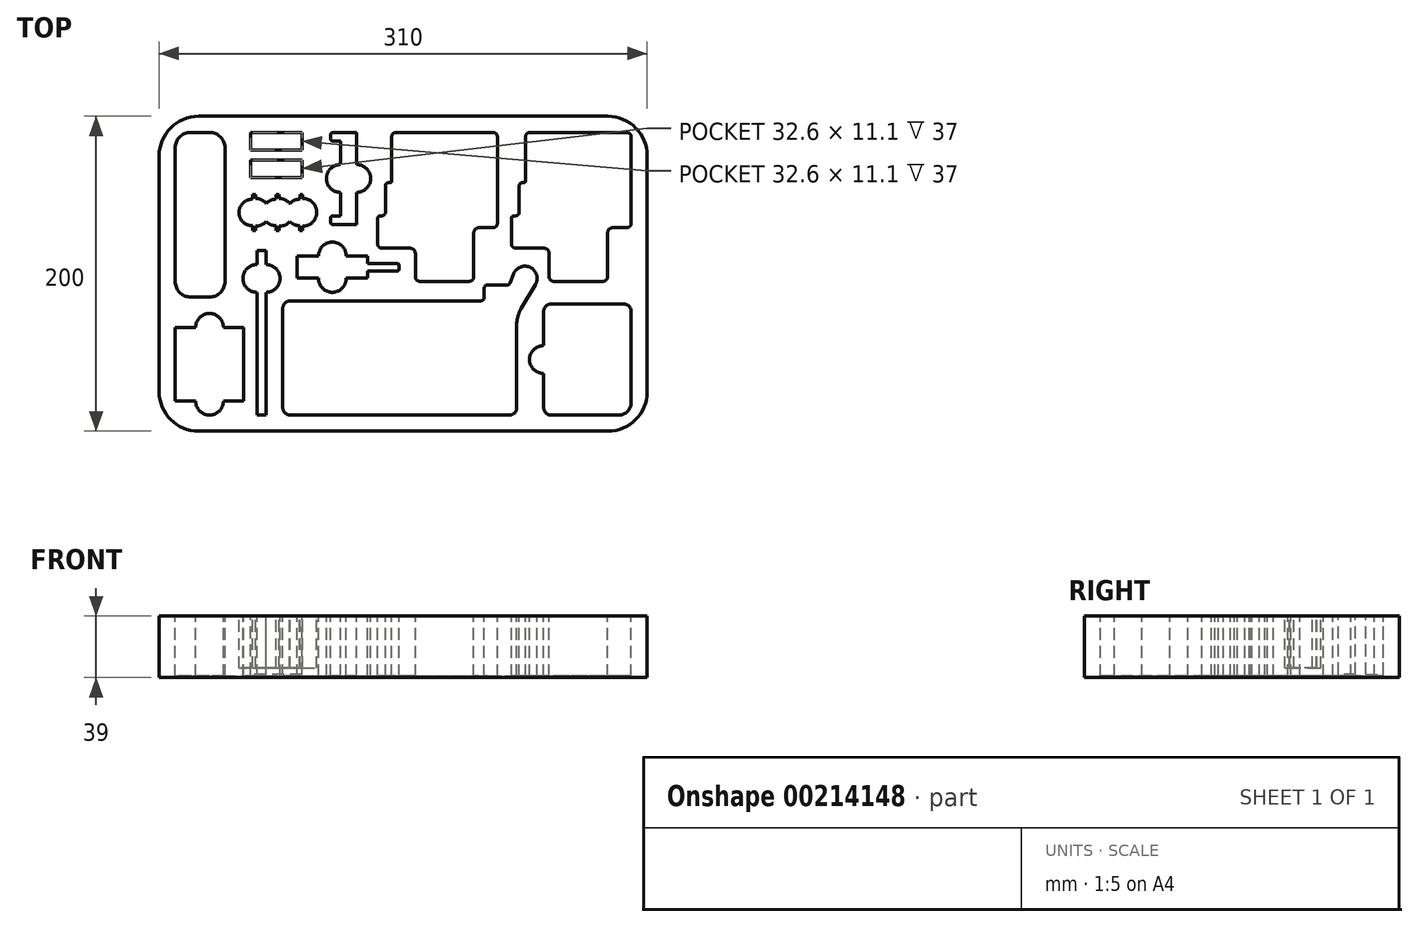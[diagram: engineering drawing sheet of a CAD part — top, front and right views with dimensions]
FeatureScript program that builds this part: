
annotation { "Feature Type Name" : "Feature", "Feature Type Description" : "" }
export const myFeature = defineFeature(function(context is Context, id is Id, definition is map)
    precondition{}
    {
        {
            var Q0;
            Q0=qCreatedBy(makeId("Top.planeOp"),FACE);
            var sketch = newSketch(context, id + "F0", { "sketchPlane" : qUnion([Q0])});
            skLineSegment(sketch, "E0.bottom", {"start": v(178, 118) * mm, "end": v(-82, 118) * mm});
            skLineSegment(sketch, "E0.top", {"start": v(178, -82) * mm, "end": v(-82, -82) * mm});
            skLineSegment(sketch, "E0.left", {"start": v(203, 93) * mm, "end": v(203, -57) * mm});
            skLineSegment(sketch, "E0.right", {"start": v(-107, 93) * mm, "end": v(-107, -57) * mm});
            skPoint(sketch, "E0.middle", {"position": v(0, 0) * mm});
            skPoint(sketch, "E1.visualSharp", {"position": v(-107, 118) * mm});
            skArc(sketch, "E1.filletArc", {"start": v(-82, 118) * mm, "mid": v(-99.68, 110.68) * mm, "end": v(-107, 93) * mm});
            skPoint(sketch, "E2.visualSharp", {"position": v(203, 118) * mm});
            skArc(sketch, "E2.filletArc", {"start": v(203, 93) * mm, "mid": v(195.68, 110.68) * mm, "end": v(178, 118) * mm});
            skPoint(sketch, "E3.visualSharp", {"position": v(-107, -82) * mm});
            skArc(sketch, "E3.filletArc", {"start": v(-107, -57) * mm, "mid": v(-99.68, -74.68) * mm, "end": v(-82, -82) * mm});
            skPoint(sketch, "E4.visualSharp", {"position": v(203, -82) * mm});
            skArc(sketch, "E4.filletArc", {"start": v(178, -82) * mm, "mid": v(195.68, -74.68) * mm, "end": v(203, -57) * mm});
            skSolve(sketch);
        }
        {
            var Q0;
            Q0=makeQuery(id+"F0.imprint","IMPRINT",FACE,{"disambiguationData":[TD([[makeQuery(id+"F0.imprint","IMPRINT",EDGE,{"derivedFrom":sQuery(id+"F0.wireOp",EDGE,"E0.bottom")}),1.0]])]});
            extrude(context, id + "F1", {"entities" : qUnion([Q0]), "oppositeDirection" : true, "depth" : 39 * mm});
        }
        {
            var Q0;
            Q0=makeQuery(id+"F1.opExtrude","CAP_FACE",FACE,{"disambiguationData":[OSD([sQuery(id+"F0.wireOp",EDGE,"E0.bottom"),sQuery(id+"F0.wireOp",EDGE,"E0.top"),sQuery(id+"F0.wireOp",EDGE,"E0.left"),sQuery(id+"F0.wireOp",EDGE,"E0.right"),sQuery(id+"F0.wireOp",EDGE,"E1.filletArc"),sQuery(id+"F0.wireOp",EDGE,"E2.filletArc"),sQuery(id+"F0.wireOp",EDGE,"E3.filletArc"),sQuery(id+"F0.wireOp",EDGE,"E4.filletArc")])],"isStart":true});
            var sketch = newSketch(context, id + "F2", { "sketchPlane" : qUnion([Q0])});
            skLineSegment(sketch, "E5.bottom", {"start": v(193, -64) * mm, "end": v(193, -6) * mm});
            skLineSegment(sketch, "E5.top", {"start": v(137, -67) * mm, "end": v(137, -45.5) * mm});
            skLineSegment(sketch, "E5.left", {"start": v(185, -72) * mm, "end": v(142, -72) * mm});
            skLineSegment(sketch, "E5.right", {"start": v(188, -1) * mm, "end": v(142, -1) * mm});
            skPoint(sketch, "E6.visualSharp", {"position": v(137, -72) * mm});
            skArc(sketch, "E6.filletArc", {"start": v(137, -67) * mm, "mid": v(138.46, -70.54) * mm, "end": v(142, -72) * mm});
            skPoint(sketch, "E7.visualSharp", {"position": v(193, -72) * mm});
            skArc(sketch, "E7.filletArc", {"start": v(185, -72) * mm, "mid": v(190.66, -69.66) * mm, "end": v(193, -64) * mm});
            skPoint(sketch, "E8.visualSharp", {"position": v(193, -1) * mm});
            skArc(sketch, "E8.filletArc", {"start": v(193, -6) * mm, "mid": v(191.54, -2.46) * mm, "end": v(188, -1) * mm});
            skPoint(sketch, "E9.visualSharp", {"position": v(137, -1) * mm});
            skArc(sketch, "E9.filletArc", {"start": v(142, -1) * mm, "mid": v(138.46, -2.46) * mm, "end": v(137, -6) * mm});
            skArc(sketch, "E10", {"start": v(137, -27.5) * mm, "mid": v(128, -36.5) * mm, "end": v(137, -45.5) * mm});
            skLineSegment(sketch, "E11.trimOffspring", {"start": v(137, -27.5) * mm, "end": v(137, -6) * mm});
            skArc(sketch, "E12.0", {"start": v(137.2, -27.7) * mm, "mid": v(128.2, -36.5) * mm, "end": v(137.2, -45.3) * mm});
            skLineSegment(sketch, "E12.1", {"start": v(137.2, -67) * mm, "end": v(137.2, -45.3) * mm});
            skLineSegment(sketch, "E12.2", {"start": v(137.2, -27.7) * mm, "end": v(137.2, -6) * mm});
            skArc(sketch, "E12.3", {"start": v(137.2, -67) * mm, "mid": v(138.6, -70.4) * mm, "end": v(142, -71.8) * mm});
            skLineSegment(sketch, "E12.4", {"start": v(185, -71.8) * mm, "end": v(142, -71.8) * mm});
            skArc(sketch, "E12.5", {"start": v(185, -71.8) * mm, "mid": v(190.52, -69.52) * mm, "end": v(192.8, -64) * mm});
            skArc(sketch, "E12.6", {"start": v(142, -1.2) * mm, "mid": v(138.6, -2.6) * mm, "end": v(137.2, -6) * mm});
            skLineSegment(sketch, "E12.7", {"start": v(188, -1.2) * mm, "end": v(142, -1.2) * mm});
            skArc(sketch, "E12.8", {"start": v(192.8, -6) * mm, "mid": v(191.4, -2.6) * mm, "end": v(188, -1.2) * mm});
            skLineSegment(sketch, "E12.9", {"start": v(192.8, -64) * mm, "end": v(192.8, -6) * mm});
            skSolve(sketch);
        }
        {
            var Q0;
            Q0=makeQuery(id+"F2.imprint","IMPRINT",FACE,{"disambiguationData":[TD([[makeQuery(id+"F2.imprint","IMPRINT",EDGE,{"derivedFrom":sQuery(id+"F2.wireOp",EDGE,"E12.0")}),1.0]])]});
            extrude(context, id + "F3", {"entities" : qUnion([Q0]), "operationType" : NewBodyOperationType.REMOVE, "oppositeDirection" : true, "depth" : 38 * mm});
        }
        {
            var Q0;
            Q0=makeQuery(id+"F1.opExtrude","CAP_FACE",FACE,{"disambiguationData":[OSD([sQuery(id+"F0.wireOp",EDGE,"E0.bottom"),sQuery(id+"F0.wireOp",EDGE,"E0.top"),sQuery(id+"F0.wireOp",EDGE,"E0.left"),sQuery(id+"F0.wireOp",EDGE,"E0.right"),sQuery(id+"F0.wireOp",EDGE,"E1.filletArc"),sQuery(id+"F0.wireOp",EDGE,"E2.filletArc"),sQuery(id+"F0.wireOp",EDGE,"E3.filletArc"),sQuery(id+"F0.wireOp",EDGE,"E4.filletArc")])],"isStart":true});
            var sketch = newSketch(context, id + "F4", { "sketchPlane" : qUnion([Q0])});
            skLineSegment(sketch, "E13.bottom", {"start": v(128.5, 108) * mm, "end": v(190, 108) * mm});
            skLineSegment(sketch, "E13.left", {"start": v(125.5, 105) * mm, "end": v(125.5, 77) * mm});
            skLineSegment(sketch, "E13.right", {"start": v(193, 105) * mm, "end": v(193, 50) * mm});
            skLineSegment(sketch, "E14.bottom", {"start": v(124.5, 76) * mm, "end": v(123.5, 76) * mm});
            skLineSegment(sketch, "E14.right", {"start": v(121.5, 74) * mm, "end": v(121.5, 57) * mm});
            skLineSegment(sketch, "E15.top", {"start": v(143.5, 13) * mm, "end": v(175, 13) * mm});
            skLineSegment(sketch, "E15.right", {"start": v(178, 44) * mm, "end": v(178, 16) * mm});
            skLineSegment(sketch, "E16.bottom", {"start": v(137.5, 34) * mm, "end": v(119.5, 34) * mm});
            skLineSegment(sketch, "E16.top", {"start": v(119.5, 55) * mm, "end": v(118.5, 55) * mm});
            skLineSegment(sketch, "E16.right", {"start": v(116.5, 37) * mm, "end": v(116.5, 53) * mm});
            skLineSegment(sketch, "E17.trimOffspring", {"start": v(140.5, 31) * mm, "end": v(140.5, 16) * mm});
            skLineSegment(sketch, "E18.trimOffspring", {"start": v(181, 47) * mm, "end": v(190, 47) * mm});
            skPoint(sketch, "E19.visualSharp", {"position": v(193, 108) * mm});
            skArc(sketch, "E19.filletArc", {"start": v(193, 105) * mm, "mid": v(192.12, 107.12) * mm, "end": v(190, 108) * mm});
            skPoint(sketch, "E20.visualSharp", {"position": v(193, 47) * mm});
            skArc(sketch, "E20.filletArc", {"start": v(190, 47) * mm, "mid": v(192.12, 47.88) * mm, "end": v(193, 50) * mm});
            skPoint(sketch, "E21.visualSharp", {"position": v(178, 47) * mm});
            skArc(sketch, "E21.filletArc", {"start": v(181, 47) * mm, "mid": v(178.88, 46.12) * mm, "end": v(178, 44) * mm});
            skPoint(sketch, "E22.visualSharp", {"position": v(178, 13) * mm});
            skArc(sketch, "E22.filletArc", {"start": v(175, 13) * mm, "mid": v(177.12, 13.88) * mm, "end": v(178, 16) * mm});
            skPoint(sketch, "E23.visualSharp", {"position": v(140.5, 13) * mm});
            skArc(sketch, "E23.filletArc", {"start": v(140.5, 16) * mm, "mid": v(141.38, 13.88) * mm, "end": v(143.5, 13) * mm});
            skPoint(sketch, "E24.visualSharp", {"position": v(140.5, 34) * mm});
            skArc(sketch, "E24.filletArc", {"start": v(140.5, 31) * mm, "mid": v(139.62, 33.12) * mm, "end": v(137.5, 34) * mm});
            skPoint(sketch, "E25.visualSharp", {"position": v(116.5, 34) * mm});
            skArc(sketch, "E25.filletArc", {"start": v(116.5, 37) * mm, "mid": v(117.38, 34.88) * mm, "end": v(119.5, 34) * mm});
            skPoint(sketch, "E26.visualSharp", {"position": v(116.5, 55) * mm});
            skArc(sketch, "E26.filletArc", {"start": v(118.5, 55) * mm, "mid": v(117.09, 54.41) * mm, "end": v(116.5, 53) * mm});
            skPoint(sketch, "E27.visualSharp", {"position": v(121.5, 76) * mm});
            skArc(sketch, "E27.filletArc", {"start": v(123.5, 76) * mm, "mid": v(122.09, 75.41) * mm, "end": v(121.5, 74) * mm});
            skPoint(sketch, "E28.visualSharp", {"position": v(125.5, 108) * mm});
            skArc(sketch, "E28.filletArc", {"start": v(128.5, 108) * mm, "mid": v(126.38, 107.12) * mm, "end": v(125.5, 105) * mm});
            skPoint(sketch, "E29.visualSharp", {"position": v(121.5, 55) * mm});
            skArc(sketch, "E29.filletArc", {"start": v(119.5, 55) * mm, "mid": v(120.91, 55.59) * mm, "end": v(121.5, 57) * mm});
            skPoint(sketch, "E30.visualSharp", {"position": v(125.5, 76) * mm});
            skArc(sketch, "E30.filletArc", {"start": v(124.5, 76) * mm, "mid": v(125.2, 76.3) * mm, "end": v(125.5, 77) * mm});
            skArc(sketch, "E31.0", {"start": v(128.5, 107.8) * mm, "mid": v(126.52, 106.98) * mm, "end": v(125.7, 105) * mm});
            skLineSegment(sketch, "E31.1", {"start": v(140.7, 31) * mm, "end": v(140.7, 16) * mm});
            skArc(sketch, "E31.2", {"start": v(140.7, 16) * mm, "mid": v(141.52, 14.02) * mm, "end": v(143.5, 13.2) * mm});
            skLineSegment(sketch, "E31.3", {"start": v(143.5, 13.2) * mm, "end": v(175, 13.2) * mm});
            skArc(sketch, "E31.4", {"start": v(175, 13.2) * mm, "mid": v(176.98, 14.02) * mm, "end": v(177.8, 16) * mm});
            skLineSegment(sketch, "E31.5", {"start": v(177.8, 44) * mm, "end": v(177.8, 16) * mm});
            skArc(sketch, "E31.6", {"start": v(181, 47.2) * mm, "mid": v(178.74, 46.26) * mm, "end": v(177.8, 44) * mm});
            skArc(sketch, "E31.7", {"start": v(192.8, 105) * mm, "mid": v(191.98, 106.98) * mm, "end": v(190, 107.8) * mm});
            skLineSegment(sketch, "E31.8", {"start": v(192.8, 105) * mm, "end": v(192.8, 50) * mm});
            skArc(sketch, "E31.9", {"start": v(190, 47.2) * mm, "mid": v(191.98, 48.02) * mm, "end": v(192.8, 50) * mm});
            skLineSegment(sketch, "E31.10", {"start": v(181, 47.2) * mm, "end": v(190, 47.2) * mm});
            skArc(sketch, "E31.11", {"start": v(140.7, 31) * mm, "mid": v(139.76, 33.26) * mm, "end": v(137.5, 34.2) * mm});
            skLineSegment(sketch, "E31.12", {"start": v(128.5, 107.8) * mm, "end": v(190, 107.8) * mm});
            skLineSegment(sketch, "E31.13", {"start": v(137.5, 34.2) * mm, "end": v(119.5, 34.2) * mm});
            skArc(sketch, "E31.14", {"start": v(116.7, 37) * mm, "mid": v(117.52, 35.02) * mm, "end": v(119.5, 34.2) * mm});
            skLineSegment(sketch, "E31.15", {"start": v(116.7, 37) * mm, "end": v(116.7, 53) * mm});
            skArc(sketch, "E31.16", {"start": v(118.5, 54.8) * mm, "mid": v(117.23, 54.27) * mm, "end": v(116.7, 53) * mm});
            skLineSegment(sketch, "E31.17", {"start": v(119.5, 54.8) * mm, "end": v(118.5, 54.8) * mm});
            skArc(sketch, "E31.18", {"start": v(119.5, 54.8) * mm, "mid": v(121.06, 55.44) * mm, "end": v(121.7, 57) * mm});
            skLineSegment(sketch, "E31.19", {"start": v(121.7, 74) * mm, "end": v(121.7, 57) * mm});
            skArc(sketch, "E31.20", {"start": v(123.5, 75.8) * mm, "mid": v(122.23, 75.27) * mm, "end": v(121.7, 74) * mm});
            skLineSegment(sketch, "E31.21", {"start": v(124.5, 75.8) * mm, "end": v(123.5, 75.8) * mm});
            skArc(sketch, "E31.22", {"start": v(124.5, 75.8) * mm, "mid": v(125.35, 76.15) * mm, "end": v(125.7, 77) * mm});
            skLineSegment(sketch, "E31.23", {"start": v(125.7, 105) * mm, "end": v(125.7, 77) * mm});
            skLineSegment(sketch, "E32.1.0.0", {"start": v(43.5, 107.8) * mm, "end": v(105, 107.8) * mm});
            skArc(sketch, "E32.1.0.1", {"start": v(43.5, 107.8) * mm, "mid": v(41.52, 106.98) * mm, "end": v(40.7, 105) * mm});
            skLineSegment(sketch, "E32.1.0.2", {"start": v(40.7, 105) * mm, "end": v(40.7, 77) * mm});
            skArc(sketch, "E32.1.0.3", {"start": v(39.5, 75.8) * mm, "mid": v(40.35, 76.15) * mm, "end": v(40.7, 77) * mm});
            skLineSegment(sketch, "E32.1.0.4", {"start": v(39.5, 75.8) * mm, "end": v(38.5, 75.8) * mm});
            skArc(sketch, "E32.1.0.5", {"start": v(38.5, 75.8) * mm, "mid": v(37.23, 75.27) * mm, "end": v(36.7, 74) * mm});
            skLineSegment(sketch, "E32.1.0.6", {"start": v(36.7, 74) * mm, "end": v(36.7, 57) * mm});
            skArc(sketch, "E32.1.0.7", {"start": v(34.5, 54.8) * mm, "mid": v(36.06, 55.44) * mm, "end": v(36.7, 57) * mm});
            skLineSegment(sketch, "E32.1.0.8", {"start": v(34.5, 54.8) * mm, "end": v(33.5, 54.8) * mm});
            skArc(sketch, "E32.1.0.9", {"start": v(33.5, 54.8) * mm, "mid": v(32.23, 54.27) * mm, "end": v(31.7, 53) * mm});
            skLineSegment(sketch, "E32.1.0.10", {"start": v(31.7, 37) * mm, "end": v(31.7, 53) * mm});
            skArc(sketch, "E32.1.0.11", {"start": v(31.7, 37) * mm, "mid": v(32.52, 35.02) * mm, "end": v(34.5, 34.2) * mm});
            skLineSegment(sketch, "E32.1.0.12", {"start": v(52.5, 34.2) * mm, "end": v(34.5, 34.2) * mm});
            skArc(sketch, "E32.1.0.13", {"start": v(55.7, 31) * mm, "mid": v(54.76, 33.26) * mm, "end": v(52.5, 34.2) * mm});
            skLineSegment(sketch, "E32.1.0.14", {"start": v(55.7, 31) * mm, "end": v(55.7, 16) * mm});
            skArc(sketch, "E32.1.0.15", {"start": v(55.7, 16) * mm, "mid": v(56.52, 14.02) * mm, "end": v(58.5, 13.2) * mm});
            skLineSegment(sketch, "E32.1.0.16", {"start": v(58.5, 13.2) * mm, "end": v(90, 13.2) * mm});
            skArc(sketch, "E32.1.0.17", {"start": v(90, 13.2) * mm, "mid": v(91.98, 14.02) * mm, "end": v(92.8, 16) * mm});
            skLineSegment(sketch, "E32.1.0.18", {"start": v(92.8, 44) * mm, "end": v(92.8, 16) * mm});
            skArc(sketch, "E32.1.0.19", {"start": v(96, 47.2) * mm, "mid": v(93.74, 46.26) * mm, "end": v(92.8, 44) * mm});
            skLineSegment(sketch, "E32.1.0.20", {"start": v(96, 47.2) * mm, "end": v(105, 47.2) * mm});
            skArc(sketch, "E32.1.0.21", {"start": v(105, 47.2) * mm, "mid": v(106.98, 48.02) * mm, "end": v(107.8, 50) * mm});
            skLineSegment(sketch, "E32.1.0.22", {"start": v(107.8, 105) * mm, "end": v(107.8, 50) * mm});
            skArc(sketch, "E32.1.0.23", {"start": v(107.8, 105) * mm, "mid": v(106.98, 106.98) * mm, "end": v(105, 107.8) * mm});
            skLineSegment(sketch, "E32.direction1", {"start": v(119.5, 34.2) * mm, "end": v(34.5, 34.2) * mm, "construction": true});
            skSolve(sketch);
        }
        {
            var Q0;
            Q0=makeQuery(id+"F4.imprint","IMPRINT",FACE,{"disambiguationData":[TD([[makeQuery(id+"F4.imprint","IMPRINT",EDGE,{"derivedFrom":sQuery(id+"F4.wireOp",EDGE,"E31.0")}),1.0]])]});
            var Q1;
            Q1=makeQuery(id+"F4.imprint","IMPRINT",FACE,{"disambiguationData":[TD([[makeQuery(id+"F4.imprint","IMPRINT",EDGE,{"derivedFrom":sQuery(id+"F4.wireOp",EDGE,"E32.1.0.0")}),-1.0]])]});
            extrude(context, id + "F5", {"entities" : qUnion([Q0, Q1]), "operationType" : NewBodyOperationType.REMOVE, "oppositeDirection" : true, "depth" : 38 * mm});
        }
        {
            var Q0;
            Q0=makeQuery(id+"F1.opExtrude","CAP_FACE",FACE,{"disambiguationData":[OSD([sQuery(id+"F0.wireOp",EDGE,"E0.bottom"),sQuery(id+"F0.wireOp",EDGE,"E0.top"),sQuery(id+"F0.wireOp",EDGE,"E0.left"),sQuery(id+"F0.wireOp",EDGE,"E0.right"),sQuery(id+"F0.wireOp",EDGE,"E1.filletArc"),sQuery(id+"F0.wireOp",EDGE,"E2.filletArc"),sQuery(id+"F0.wireOp",EDGE,"E3.filletArc"),sQuery(id+"F0.wireOp",EDGE,"E4.filletArc")])],"isStart":true});
            var sketch = newSketch(context, id + "F6", { "sketchPlane" : qUnion([Q0])});
            skLineSegment(sketch, "E33.bottom", {"start": v(-19.5, 15) * mm, "end": v(-6, 15) * mm});
            skLineSegment(sketch, "E33.top", {"start": v(-19.5, 29.3) * mm, "end": v(-6, 29.3) * mm});
            skLineSegment(sketch, "E33.left", {"start": v(-19.5, 15) * mm, "end": v(-19.5, 29.3) * mm});
            skLineSegment(sketch, "E33.right", {"start": v(25.5, 15) * mm, "end": v(25.5, 19.65) * mm});
            skLineSegment(sketch, "E34.bottom", {"start": v(25.5, 19.65) * mm, "end": v(44.5, 19.65) * mm});
            skLineSegment(sketch, "E34.top", {"start": v(25.5, 24.65) * mm, "end": v(44.5, 24.65) * mm});
            skLineSegment(sketch, "E34.right", {"start": v(45.5, 20.65) * mm, "end": v(45.5, 23.65) * mm});
            skLineSegment(sketch, "E35.trimOffspring", {"start": v(25.5, 24.65) * mm, "end": v(25.5, 29.3) * mm});
            skArc(sketch, "E36", {"start": v(12, 29.3) * mm, "mid": v(3, 38.3) * mm, "end": v(-6, 29.3) * mm});
            skArc(sketch, "E37", {"start": v(-6, 15) * mm, "mid": v(3, 6) * mm, "end": v(12, 15) * mm});
            skPoint(sketch, "E38.visualSharp", {"position": v(45.5, 24.65) * mm});
            skArc(sketch, "E38.filletArc", {"start": v(45.5, 23.65) * mm, "mid": v(45.2, 24.36) * mm, "end": v(44.5, 24.65) * mm});
            skPoint(sketch, "E39.visualSharp", {"position": v(45.5, 19.65) * mm});
            skArc(sketch, "E39.filletArc", {"start": v(44.5, 19.65) * mm, "mid": v(45.2, 19.94) * mm, "end": v(45.5, 20.65) * mm});
            skLineSegment(sketch, "E40.trimOffspring", {"start": v(12, 29.3) * mm, "end": v(25.5, 29.3) * mm});
            skLineSegment(sketch, "E41.trimOffspring", {"start": v(12, 15) * mm, "end": v(25.5, 15) * mm});
            skLineSegment(sketch, "E42.0", {"start": v(11.8, 29.1) * mm, "end": v(25.3, 29.1) * mm});
            skLineSegment(sketch, "E42.1", {"start": v(25.3, 24.45) * mm, "end": v(25.3, 29.1) * mm});
            skLineSegment(sketch, "E42.2", {"start": v(25.3, 24.45) * mm, "end": v(44.5, 24.45) * mm});
            skArc(sketch, "E42.3", {"start": v(-5.8, 15.2) * mm, "mid": v(3, 6.2) * mm, "end": v(11.8, 15.2) * mm});
            skLineSegment(sketch, "E42.4", {"start": v(-19.3, 15.2) * mm, "end": v(-5.8, 15.2) * mm});
            skLineSegment(sketch, "E42.5", {"start": v(-19.3, 15.2) * mm, "end": v(-19.3, 29.1) * mm});
            skLineSegment(sketch, "E42.6", {"start": v(-19.3, 29.1) * mm, "end": v(-5.8, 29.1) * mm});
            skLineSegment(sketch, "E42.7", {"start": v(11.8, 15.2) * mm, "end": v(25.3, 15.2) * mm});
            skLineSegment(sketch, "E42.8", {"start": v(25.3, 15.2) * mm, "end": v(25.3, 19.85) * mm});
            skLineSegment(sketch, "E42.9", {"start": v(25.3, 19.85) * mm, "end": v(44.5, 19.85) * mm});
            skArc(sketch, "E42.10", {"start": v(11.8, 29.1) * mm, "mid": v(3, 38.1) * mm, "end": v(-5.8, 29.1) * mm});
            skArc(sketch, "E42.11", {"start": v(44.5, 19.85) * mm, "mid": v(45.07, 20.08) * mm, "end": v(45.3, 20.65) * mm});
            skLineSegment(sketch, "E42.12", {"start": v(45.3, 20.65) * mm, "end": v(45.3, 23.65) * mm});
            skArc(sketch, "E42.13", {"start": v(45.3, 23.65) * mm, "mid": v(45.07, 24.22) * mm, "end": v(44.5, 24.45) * mm});
            skSolve(sketch);
        }
        {
            var Q0;
            Q0=makeQuery(id+"F6.imprint","IMPRINT",FACE,{"disambiguationData":[TD([[makeQuery(id+"F6.imprint","IMPRINT",EDGE,{"derivedFrom":sQuery(id+"F6.wireOp",EDGE,"E42.0")}),-1.0]])]});
            extrude(context, id + "F7", {"entities" : qUnion([Q0]), "operationType" : NewBodyOperationType.REMOVE, "oppositeDirection" : true, "depth" : 38 * mm});
        }
        {
            var Q0;
            Q0=makeQuery(id+"F1.opExtrude","CAP_FACE",FACE,{"disambiguationData":[OSD([sQuery(id+"F0.wireOp",EDGE,"E0.bottom"),sQuery(id+"F0.wireOp",EDGE,"E0.top"),sQuery(id+"F0.wireOp",EDGE,"E0.left"),sQuery(id+"F0.wireOp",EDGE,"E0.right"),sQuery(id+"F0.wireOp",EDGE,"E1.filletArc"),sQuery(id+"F0.wireOp",EDGE,"E2.filletArc"),sQuery(id+"F0.wireOp",EDGE,"E3.filletArc"),sQuery(id+"F0.wireOp",EDGE,"E4.filletArc")])],"isStart":true});
            var sketch = newSketch(context, id + "F8", { "sketchPlane" : qUnion([Q0])});
            skLineSegment(sketch, "E43.bottom", {"start": v(-45, 33) * mm, "end": v(-45, 24) * mm});
            skLineSegment(sketch, "E43.top", {"start": v(-39, 33) * mm, "end": v(-39, 24) * mm});
            skLineSegment(sketch, "E43.left", {"start": v(-45, 33) * mm, "end": v(-39, 33) * mm});
            skLineSegment(sketch, "E43.right", {"start": v(-45, -72) * mm, "end": v(-39, -72) * mm});
            skArc(sketch, "E44", {"start": v(-39, 6) * mm, "mid": v(-30, 15) * mm, "end": v(-39, 24) * mm});
            skArc(sketch, "E45", {"start": v(-45, 24) * mm, "mid": v(-54, 15) * mm, "end": v(-45, 6) * mm});
            skLineSegment(sketch, "E46.trimOffspring", {"start": v(-45, 6) * mm, "end": v(-45, -72) * mm});
            skLineSegment(sketch, "E47.trimOffspring", {"start": v(-39, 6) * mm, "end": v(-39, -72) * mm});
            skLineSegment(sketch, "E48.0", {"start": v(-44.8, 32.8) * mm, "end": v(-44.8, 23.8) * mm});
            skArc(sketch, "E48.1", {"start": v(-44.8, 23.8) * mm, "mid": v(-53.8, 15) * mm, "end": v(-44.8, 6.2) * mm});
            skLineSegment(sketch, "E48.2", {"start": v(-44.8, 32.8) * mm, "end": v(-39.2, 32.8) * mm});
            skLineSegment(sketch, "E48.3", {"start": v(-44.8, 6.2) * mm, "end": v(-44.8, -71.8) * mm});
            skLineSegment(sketch, "E48.4", {"start": v(-39.2, 32.8) * mm, "end": v(-39.2, 23.8) * mm});
            skArc(sketch, "E48.5", {"start": v(-39.2, 6.2) * mm, "mid": v(-30.2, 15) * mm, "end": v(-39.2, 23.8) * mm});
            skLineSegment(sketch, "E48.6", {"start": v(-39.2, 6.2) * mm, "end": v(-39.2, -71.8) * mm});
            skLineSegment(sketch, "E48.7", {"start": v(-44.8, -71.8) * mm, "end": v(-39.2, -71.8) * mm});
            skSolve(sketch);
        }
        {
            var Q0;
            Q0=makeQuery(id+"F8.imprint","IMPRINT",FACE,{"disambiguationData":[TD([[makeQuery(id+"F8.imprint","IMPRINT",EDGE,{"derivedFrom":sQuery(id+"F8.wireOp",EDGE,"E48.0")}),1.0]])]});
            extrude(context, id + "F9", {"entities" : qUnion([Q0]), "operationType" : NewBodyOperationType.REMOVE, "oppositeDirection" : true, "depth" : 38 * mm});
        }
        {
            var Q0;
            Q0=makeQuery(id+"F1.opExtrude","CAP_FACE",FACE,{"disambiguationData":[OSD([sQuery(id+"F0.wireOp",EDGE,"E0.bottom"),sQuery(id+"F0.wireOp",EDGE,"E0.top"),sQuery(id+"F0.wireOp",EDGE,"E0.left"),sQuery(id+"F0.wireOp",EDGE,"E0.right"),sQuery(id+"F0.wireOp",EDGE,"E1.filletArc"),sQuery(id+"F0.wireOp",EDGE,"E2.filletArc"),sQuery(id+"F0.wireOp",EDGE,"E3.filletArc"),sQuery(id+"F0.wireOp",EDGE,"E4.filletArc")])],"isStart":true});
            var sketch = newSketch(context, id + "F10", { "sketchPlane" : qUnion([Q0])});
            skLineSegment(sketch, "E49.bottom", {"start": v(-65, 13) * mm, "end": v(-65, 98) * mm});
            skLineSegment(sketch, "E49.top", {"start": v(-97, 13) * mm, "end": v(-97, 98) * mm});
            skLineSegment(sketch, "E49.left", {"start": v(-75, 3) * mm, "end": v(-87, 3) * mm});
            skLineSegment(sketch, "E49.right", {"start": v(-75, 108) * mm, "end": v(-87, 108) * mm});
            skPoint(sketch, "E50.visualSharp", {"position": v(-97, 108) * mm});
            skArc(sketch, "E50.filletArc", {"start": v(-87, 108) * mm, "mid": v(-94.07, 105.07) * mm, "end": v(-97, 98) * mm});
            skPoint(sketch, "E51.visualSharp", {"position": v(-65, 108) * mm});
            skArc(sketch, "E51.filletArc", {"start": v(-65, 98) * mm, "mid": v(-67.93, 105.07) * mm, "end": v(-75, 108) * mm});
            skPoint(sketch, "E52.visualSharp", {"position": v(-65, 3) * mm});
            skArc(sketch, "E52.filletArc", {"start": v(-75, 3) * mm, "mid": v(-67.93, 5.93) * mm, "end": v(-65, 13) * mm});
            skPoint(sketch, "E53.visualSharp", {"position": v(-97, 3) * mm});
            skArc(sketch, "E53.filletArc", {"start": v(-97, 13) * mm, "mid": v(-94.07, 5.93) * mm, "end": v(-87, 3) * mm});
            skArc(sketch, "E54.0", {"start": v(-65.2, 98) * mm, "mid": v(-68.07, 104.93) * mm, "end": v(-75, 107.8) * mm});
            skLineSegment(sketch, "E54.1", {"start": v(-65.2, 13) * mm, "end": v(-65.2, 98) * mm});
            skLineSegment(sketch, "E54.2", {"start": v(-75, 107.8) * mm, "end": v(-87, 107.8) * mm});
            skArc(sketch, "E54.3", {"start": v(-75, 3.2) * mm, "mid": v(-68.07, 6.07) * mm, "end": v(-65.2, 13) * mm});
            skArc(sketch, "E54.4", {"start": v(-87, 107.8) * mm, "mid": v(-93.93, 104.93) * mm, "end": v(-96.8, 98) * mm});
            skLineSegment(sketch, "E54.5", {"start": v(-96.8, 13) * mm, "end": v(-96.8, 98) * mm});
            skArc(sketch, "E54.6", {"start": v(-96.8, 13) * mm, "mid": v(-93.93, 6.07) * mm, "end": v(-87, 3.2) * mm});
            skLineSegment(sketch, "E54.7", {"start": v(-75, 3.2) * mm, "end": v(-87, 3.2) * mm});
            skSolve(sketch);
        }
        {
            var Q0;
            Q0=makeQuery(id+"F10.imprint","IMPRINT",FACE,{"disambiguationData":[TD([[makeQuery(id+"F10.imprint","IMPRINT",EDGE,{"derivedFrom":sQuery(id+"F10.wireOp",EDGE,"E54.0")}),1.0]])]});
            extrude(context, id + "F11", {"entities" : qUnion([Q0]), "operationType" : NewBodyOperationType.REMOVE, "oppositeDirection" : true, "depth" : 38 * mm});
        }
        {
            var Q0;
            Q0=makeQuery(id+"F1.opExtrude","CAP_FACE",FACE,{"disambiguationData":[OSD([sQuery(id+"F0.wireOp",EDGE,"E0.bottom"),sQuery(id+"F0.wireOp",EDGE,"E0.top"),sQuery(id+"F0.wireOp",EDGE,"E0.left"),sQuery(id+"F0.wireOp",EDGE,"E0.right"),sQuery(id+"F0.wireOp",EDGE,"E1.filletArc"),sQuery(id+"F0.wireOp",EDGE,"E2.filletArc"),sQuery(id+"F0.wireOp",EDGE,"E3.filletArc"),sQuery(id+"F0.wireOp",EDGE,"E4.filletArc")])],"isStart":true});
            var sketch = newSketch(context, id + "F12", { "sketchPlane" : qUnion([Q0])});
            skArc(sketch, "E55.MirrorCS", {"start": v(-45.7, 66) * mm, "mid": v(-42.02, 65.21) * mm, "end": v(-38.98, 62.99) * mm});
            skLineSegment(sketch, "E56.MirrorCS", {"start": v(-45.7, 45) * mm, "end": v(-45.7, 48) * mm});
            skLineSegment(sketch, "E57.MirrorCS", {"start": v(-47.95, 45) * mm, "end": v(-47.93, 48.33) * mm});
            skLineSegment(sketch, "E58.MirrorCS", {"start": v(-48.2, 68.53) * mm, "end": v(-45.9, 68.53) * mm});
            skLineSegment(sketch, "E59.MirrorCS", {"start": v(-48.35, 45.33) * mm, "end": v(-46.05, 45.33) * mm});
            skArc(sketch, "E60.MirrorCS", {"start": v(-47.93, 48.33) * mm, "mid": v(-56.47, 56.99) * mm, "end": v(-47.82, 65.53) * mm});
            skLineSegment(sketch, "E61.1.0.0", {"start": v(-30.7, 45) * mm, "end": v(-30.7, 48) * mm});
            skLineSegment(sketch, "E61.1.0.1", {"start": v(-32.95, 45) * mm, "end": v(-32.93, 48.33) * mm});
            skArc(sketch, "E61.1.0.2", {"start": v(-32.93, 48.33) * mm, "mid": v(-36.25, 49.02) * mm, "end": v(-39.04, 50.94) * mm});
            skArc(sketch, "E61.1.0.3", {"start": v(-30.7, 66) * mm, "mid": v(-27.02, 65.21) * mm, "end": v(-23.98, 62.99) * mm});
            skLineSegment(sketch, "E61.1.0.4", {"start": v(-33.2, 68.53) * mm, "end": v(-30.9, 68.53) * mm});
            skLineSegment(sketch, "E61.1.0.5", {"start": v(-33.35, 45.33) * mm, "end": v(-31.05, 45.33) * mm});
            skLineSegment(sketch, "E61.2.0.0", {"start": v(-15.7, 45) * mm, "end": v(-15.7, 48) * mm});
            skLineSegment(sketch, "E61.2.0.1", {"start": v(-17.95, 45) * mm, "end": v(-17.93, 48.33) * mm});
            skArc(sketch, "E61.2.0.2", {"start": v(-17.93, 48.33) * mm, "mid": v(-21.25, 49.02) * mm, "end": v(-24.04, 50.94) * mm});
            skArc(sketch, "E61.2.0.3", {"start": v(-15.7, 66) * mm, "mid": v(-6.7, 57) * mm, "end": v(-15.7, 48) * mm});
            skLineSegment(sketch, "E61.2.0.4", {"start": v(-18.2, 68.53) * mm, "end": v(-15.9, 68.53) * mm});
            skLineSegment(sketch, "E61.2.0.5", {"start": v(-18.35, 45.33) * mm, "end": v(-16.05, 45.33) * mm});
            skLineSegment(sketch, "E61.direction1", {"start": v(-47.95, 45) * mm, "end": v(-32.95, 45) * mm, "construction": true});
            skLineSegment(sketch, "E62.trimOffspring", {"start": v(-47.82, 65.53) * mm, "end": v(-47.8, 68.93) * mm});
            skLineSegment(sketch, "E63.trimOffspring", {"start": v(-45.7, 66) * mm, "end": v(-45.7, 69) * mm});
            skArc(sketch, "E64.trimOffspring", {"start": v(-38.98, 62.99) * mm, "mid": v(-36.16, 64.88) * mm, "end": v(-32.82, 65.53) * mm});
            skArc(sketch, "E65.trimOffspring", {"start": v(-39.04, 50.94) * mm, "mid": v(-42.06, 48.77) * mm, "end": v(-45.7, 48) * mm});
            skLineSegment(sketch, "E66.trimOffspring", {"start": v(-32.82, 65.53) * mm, "end": v(-32.8, 68.93) * mm});
            skLineSegment(sketch, "E67.trimOffspring", {"start": v(-30.7, 66) * mm, "end": v(-30.7, 69) * mm});
            skArc(sketch, "E68.trimOffspring", {"start": v(-23.98, 62.99) * mm, "mid": v(-21.16, 64.88) * mm, "end": v(-17.82, 65.53) * mm});
            skArc(sketch, "E69.trimOffspring", {"start": v(-24.04, 50.94) * mm, "mid": v(-27.06, 48.77) * mm, "end": v(-30.7, 48) * mm});
            skLineSegment(sketch, "E70.trimOffspring", {"start": v(-17.82, 65.53) * mm, "end": v(-17.8, 68.93) * mm});
            skLineSegment(sketch, "E71.trimOffspring", {"start": v(-15.7, 66) * mm, "end": v(-15.7, 69) * mm});
            skArc(sketch, "E72.0", {"start": v(-17.73, 48.54) * mm, "mid": v(-21.18, 49.21) * mm, "end": v(-24.05, 51.24) * mm});
            skLineSegment(sketch, "E72.1", {"start": v(-17.75, 45.53) * mm, "end": v(-17.73, 48.54) * mm});
            skLineSegment(sketch, "E72.2", {"start": v(-17.75, 45.53) * mm, "end": v(-15.9, 45.53) * mm});
            skLineSegment(sketch, "E72.3", {"start": v(-15.9, 45.53) * mm, "end": v(-15.9, 48.2) * mm});
            skArc(sketch, "E72.4", {"start": v(-15.9, 65.8) * mm, "mid": v(-6.9, 57) * mm, "end": v(-15.9, 48.2) * mm});
            skLineSegment(sketch, "E72.5", {"start": v(-47.62, 65.33) * mm, "end": v(-47.6, 68.33) * mm});
            skArc(sketch, "E72.6", {"start": v(-47.73, 48.54) * mm, "mid": v(-56.27, 56.99) * mm, "end": v(-47.62, 65.33) * mm});
            skLineSegment(sketch, "E72.7", {"start": v(-47.75, 45.53) * mm, "end": v(-47.73, 48.54) * mm});
            skLineSegment(sketch, "E72.8", {"start": v(-47.75, 45.53) * mm, "end": v(-45.9, 45.53) * mm});
            skLineSegment(sketch, "E72.9", {"start": v(-45.9, 45.53) * mm, "end": v(-45.9, 48.2) * mm});
            skArc(sketch, "E72.10", {"start": v(-39.05, 51.24) * mm, "mid": v(-42.13, 48.95) * mm, "end": v(-45.9, 48.2) * mm});
            skLineSegment(sketch, "E72.11", {"start": v(-30.9, 45.53) * mm, "end": v(-30.9, 48.2) * mm});
            skLineSegment(sketch, "E72.12", {"start": v(-32.75, 45.53) * mm, "end": v(-30.9, 45.53) * mm});
            skLineSegment(sketch, "E72.13", {"start": v(-32.75, 45.53) * mm, "end": v(-32.73, 48.54) * mm});
            skArc(sketch, "E72.14", {"start": v(-32.73, 48.54) * mm, "mid": v(-36.18, 49.21) * mm, "end": v(-39.05, 51.24) * mm});
            skLineSegment(sketch, "E72.15", {"start": v(-47.6, 68.33) * mm, "end": v(-45.9, 68.33) * mm});
            skLineSegment(sketch, "E72.16", {"start": v(-45.9, 65.8) * mm, "end": v(-45.9, 68.33) * mm});
            skArc(sketch, "E72.17", {"start": v(-45.9, 65.8) * mm, "mid": v(-42.1, 65.03) * mm, "end": v(-38.99, 62.7) * mm});
            skArc(sketch, "E72.18", {"start": v(-38.99, 62.7) * mm, "mid": v(-36.09, 64.7) * mm, "end": v(-32.62, 65.33) * mm});
            skLineSegment(sketch, "E72.19", {"start": v(-32.62, 65.33) * mm, "end": v(-32.6, 68.33) * mm});
            skArc(sketch, "E72.20", {"start": v(-24.05, 51.24) * mm, "mid": v(-27.13, 48.95) * mm, "end": v(-30.9, 48.2) * mm});
            skLineSegment(sketch, "E72.21", {"start": v(-32.6, 68.33) * mm, "end": v(-30.9, 68.33) * mm});
            skLineSegment(sketch, "E72.22", {"start": v(-30.9, 65.8) * mm, "end": v(-30.9, 68.33) * mm});
            skArc(sketch, "E72.23", {"start": v(-30.9, 65.8) * mm, "mid": v(-27.1, 65.03) * mm, "end": v(-23.99, 62.7) * mm});
            skArc(sketch, "E72.24", {"start": v(-23.99, 62.7) * mm, "mid": v(-21.09, 64.7) * mm, "end": v(-17.62, 65.33) * mm});
            skLineSegment(sketch, "E72.25", {"start": v(-17.62, 65.33) * mm, "end": v(-17.6, 68.33) * mm});
            skLineSegment(sketch, "E72.26", {"start": v(-17.6, 68.33) * mm, "end": v(-15.9, 68.33) * mm});
            skLineSegment(sketch, "E72.27", {"start": v(-15.9, 65.8) * mm, "end": v(-15.9, 68.33) * mm});
            skSolve(sketch);
        }
        {
            var Q0;
            Q0 = qSketchRegion(id + "F12", true);
            extrude(context, id + "F13", {"entities" : qUnion([Q0]), "operationType" : NewBodyOperationType.REMOVE, "oppositeDirection" : true, "depth" : 33 * mm});
        }
        {
            var Q0;
            Q0=makeQuery(id+"F1.opExtrude","CAP_FACE",FACE,{"disambiguationData":[OSD([sQuery(id+"F0.wireOp",EDGE,"E0.bottom"),sQuery(id+"F0.wireOp",EDGE,"E0.top"),sQuery(id+"F0.wireOp",EDGE,"E0.left"),sQuery(id+"F0.wireOp",EDGE,"E0.right"),sQuery(id+"F0.wireOp",EDGE,"E1.filletArc"),sQuery(id+"F0.wireOp",EDGE,"E2.filletArc"),sQuery(id+"F0.wireOp",EDGE,"E3.filletArc"),sQuery(id+"F0.wireOp",EDGE,"E4.filletArc")])],"isStart":true});
            var sketch = newSketch(context, id + "F14", { "sketchPlane" : qUnion([Q0])});
            skLineSegment(sketch, "E73.bottom", {"start": v(-16, 90.5) * mm, "end": v(-49, 90.5) * mm});
            skLineSegment(sketch, "E73.top", {"start": v(-16, 79) * mm, "end": v(-49, 79) * mm});
            skLineSegment(sketch, "E73.left", {"start": v(-16, 90.5) * mm, "end": v(-16, 79) * mm});
            skLineSegment(sketch, "E73.right", {"start": v(-49, 90.5) * mm, "end": v(-49, 79) * mm});
            skLineSegment(sketch, "E74", {"start": v(-16, 90.5) * mm, "end": v(-16, 93.5) * mm, "construction": true});
            skLineSegment(sketch, "E75", {"start": v(-16, 93.5) * mm, "end": v(-49, 93.5) * mm, "construction": true});
            skLineSegment(sketch, "E76", {"start": v(-49, 93.5) * mm, "end": v(-49, 90.5) * mm, "construction": true});
            skLineSegment(sketch, "E77.MirrorCS", {"start": v(-16, 96.5) * mm, "end": v(-49, 96.5) * mm});
            skLineSegment(sketch, "E78.MirrorCS", {"start": v(-16, 108) * mm, "end": v(-49, 108) * mm});
            skLineSegment(sketch, "E79.MirrorCS", {"start": v(-16, 96.5) * mm, "end": v(-16, 108) * mm});
            skLineSegment(sketch, "E80.MirrorCS", {"start": v(-49, 96.5) * mm, "end": v(-49, 108) * mm});
            skLineSegment(sketch, "E81.0", {"start": v(-16.2, 107.8) * mm, "end": v(-48.8, 107.8) * mm});
            skLineSegment(sketch, "E81.1", {"start": v(-16.2, 96.7) * mm, "end": v(-16.2, 107.8) * mm});
            skLineSegment(sketch, "E81.2", {"start": v(-16.2, 96.7) * mm, "end": v(-48.8, 96.7) * mm});
            skLineSegment(sketch, "E81.3", {"start": v(-48.8, 96.7) * mm, "end": v(-48.8, 107.8) * mm});
            skLineSegment(sketch, "E82.0", {"start": v(-16.2, 90.3) * mm, "end": v(-48.8, 90.3) * mm});
            skLineSegment(sketch, "E82.1", {"start": v(-16.2, 90.3) * mm, "end": v(-16.2, 79.2) * mm});
            skLineSegment(sketch, "E82.2", {"start": v(-16.2, 79.2) * mm, "end": v(-48.8, 79.2) * mm});
            skLineSegment(sketch, "E82.3", {"start": v(-48.8, 90.3) * mm, "end": v(-48.8, 79.2) * mm});
            skSolve(sketch);
        }
        {
            var Q0;
            Q0=makeQuery(id+"F14.imprint","IMPRINT",FACE,{"disambiguationData":[TD([[makeQuery(id+"F14.imprint","IMPRINT",EDGE,{"derivedFrom":sQuery(id+"F14.wireOp",EDGE,"E81.0")}),1.0]])]});
            var Q1;
            Q1=makeQuery(id+"F14.imprint","IMPRINT",FACE,{"disambiguationData":[TD([[makeQuery(id+"F14.imprint","IMPRINT",EDGE,{"derivedFrom":sQuery(id+"F14.wireOp",EDGE,"E82.0")}),1.0]])]});
            extrude(context, id + "F15", {"entities" : qUnion([Q0, Q1]), "operationType" : NewBodyOperationType.REMOVE, "oppositeDirection" : true, "depth" : 37 * mm});
        }
        {
            var Q0;
            Q0=makeQuery(id+"F1.opExtrude","CAP_FACE",FACE,{"disambiguationData":[OSD([sQuery(id+"F0.wireOp",EDGE,"E0.bottom"),sQuery(id+"F0.wireOp",EDGE,"E0.top"),sQuery(id+"F0.wireOp",EDGE,"E0.left"),sQuery(id+"F0.wireOp",EDGE,"E0.right"),sQuery(id+"F0.wireOp",EDGE,"E1.filletArc"),sQuery(id+"F0.wireOp",EDGE,"E2.filletArc"),sQuery(id+"F0.wireOp",EDGE,"E3.filletArc"),sQuery(id+"F0.wireOp",EDGE,"E4.filletArc")])],"isStart":true});
            var sketch = newSketch(context, id + "F16", { "sketchPlane" : qUnion([Q0])});
            skLineSegment(sketch, "E83.bottom", {"start": v(18.53, 87.5) * mm, "end": v(18.53, 108) * mm});
            skLineSegment(sketch, "E83.top", {"start": v(8.03, 87.5) * mm, "end": v(8.03, 102) * mm});
            skLineSegment(sketch, "E83.right", {"start": v(18.53, 108) * mm, "end": v(3.53, 108) * mm});
            skLineSegment(sketch, "E84.top", {"start": v(1.53, 106) * mm, "end": v(1.53, 104) * mm});
            skLineSegment(sketch, "E84.right", {"start": v(8.03, 102) * mm, "end": v(3.53, 102) * mm});
            skLineSegment(sketch, "E85", {"start": v(8.03, 78.5) * mm, "end": v(18.53, 78.5) * mm, "construction": true});
            skPoint(sketch, "E83.left.end.orphan", {"position": v(8.03, 55) * mm});
            skPoint(sketch, "E86.orphan", {"position": v(18.53, 49) * mm});
            skLineSegment(sketch, "E87.MirrorCS", {"start": v(18.53, 69.5) * mm, "end": v(18.53, 49) * mm});
            skLineSegment(sketch, "E88.MirrorCS", {"start": v(8.03, 69.5) * mm, "end": v(8.03, 55) * mm});
            skLineSegment(sketch, "E89.MirrorCS", {"start": v(8.03, 55) * mm, "end": v(3.53, 55) * mm});
            skLineSegment(sketch, "E90.MirrorCS", {"start": v(1.53, 51) * mm, "end": v(1.53, 53) * mm});
            skLineSegment(sketch, "E91.MirrorCS", {"start": v(18.53, 49) * mm, "end": v(3.53, 49) * mm});
            skArc(sketch, "E92", {"start": v(8.03, 87.5) * mm, "mid": v(-0.97, 78.5) * mm, "end": v(8.03, 69.5) * mm});
            skArc(sketch, "E93", {"start": v(18.53, 69.5) * mm, "mid": v(27.53, 78.5) * mm, "end": v(18.53, 87.5) * mm});
            skPoint(sketch, "E94.endSnap0", {"position": v(27.53, 78.5) * mm});
            skPoint(sketch, "E95.visualSharp", {"position": v(1.53, 108) * mm});
            skArc(sketch, "E95.filletArc", {"start": v(3.53, 108) * mm, "mid": v(2.12, 107.41) * mm, "end": v(1.53, 106) * mm});
            skPoint(sketch, "E96.visualSharp", {"position": v(1.53, 49) * mm});
            skArc(sketch, "E96.filletArc", {"start": v(1.53, 51) * mm, "mid": v(2.12, 49.59) * mm, "end": v(3.53, 49) * mm});
            skPoint(sketch, "E97.visualSharp", {"position": v(1.53, 55) * mm});
            skArc(sketch, "E97.filletArc", {"start": v(3.53, 55) * mm, "mid": v(2.12, 54.41) * mm, "end": v(1.53, 53) * mm});
            skPoint(sketch, "E98.visualSharp", {"position": v(1.53, 102) * mm});
            skArc(sketch, "E98.filletArc", {"start": v(1.53, 104) * mm, "mid": v(2.12, 102.59) * mm, "end": v(3.53, 102) * mm});
            skLineSegment(sketch, "E99.0", {"start": v(18.33, 87.3) * mm, "end": v(18.33, 107.8) * mm});
            skArc(sketch, "E99.1", {"start": v(18.33, 69.7) * mm, "mid": v(27.33, 78.5) * mm, "end": v(18.33, 87.3) * mm});
            skLineSegment(sketch, "E99.2", {"start": v(18.33, 69.7) * mm, "end": v(18.33, 49.2) * mm});
            skLineSegment(sketch, "E99.3", {"start": v(18.33, 49.2) * mm, "end": v(3.53, 49.2) * mm});
            skArc(sketch, "E99.4", {"start": v(1.73, 51) * mm, "mid": v(2.26, 49.73) * mm, "end": v(3.53, 49.2) * mm});
            skLineSegment(sketch, "E99.5", {"start": v(8.23, 102.2) * mm, "end": v(3.53, 102.2) * mm});
            skArc(sketch, "E99.6", {"start": v(1.73, 104) * mm, "mid": v(2.26, 102.73) * mm, "end": v(3.53, 102.2) * mm});
            skLineSegment(sketch, "E99.7", {"start": v(1.73, 106) * mm, "end": v(1.73, 104) * mm});
            skArc(sketch, "E99.8", {"start": v(3.53, 107.8) * mm, "mid": v(2.26, 107.27) * mm, "end": v(1.73, 106) * mm});
            skLineSegment(sketch, "E99.9", {"start": v(8.23, 87.3) * mm, "end": v(8.23, 102.2) * mm});
            skArc(sketch, "E99.10", {"start": v(8.23, 87.3) * mm, "mid": v(-0.77, 78.5) * mm, "end": v(8.23, 69.7) * mm});
            skLineSegment(sketch, "E99.11", {"start": v(8.23, 69.7) * mm, "end": v(8.23, 54.8) * mm});
            skLineSegment(sketch, "E99.12", {"start": v(8.23, 54.8) * mm, "end": v(3.53, 54.8) * mm});
            skArc(sketch, "E99.13", {"start": v(3.53, 54.8) * mm, "mid": v(2.26, 54.27) * mm, "end": v(1.73, 53) * mm});
            skLineSegment(sketch, "E99.14", {"start": v(18.33, 107.8) * mm, "end": v(3.53, 107.8) * mm});
            skLineSegment(sketch, "E99.15", {"start": v(1.73, 51) * mm, "end": v(1.73, 53) * mm});
            skSolve(sketch);
        }
        {
            var Q0;
            Q0=makeQuery(id+"F16.imprint","IMPRINT",FACE,{"disambiguationData":[TD([[makeQuery(id+"F16.imprint","IMPRINT",EDGE,{"derivedFrom":sQuery(id+"F16.wireOp",EDGE,"E99.0")}),1.0]])]});
            extrude(context, id + "F17", {"entities" : qUnion([Q0]), "operationType" : NewBodyOperationType.REMOVE, "oppositeDirection" : true, "depth" : 38 * mm});
        }
        {
            var Q0;
            Q0=makeQuery(id+"F1.opExtrude","CAP_FACE",FACE,{"disambiguationData":[OSD([sQuery(id+"F0.wireOp",EDGE,"E0.bottom"),sQuery(id+"F0.wireOp",EDGE,"E0.top"),sQuery(id+"F0.wireOp",EDGE,"E0.left"),sQuery(id+"F0.wireOp",EDGE,"E0.right"),sQuery(id+"F0.wireOp",EDGE,"E1.filletArc"),sQuery(id+"F0.wireOp",EDGE,"E2.filletArc"),sQuery(id+"F0.wireOp",EDGE,"E3.filletArc"),sQuery(id+"F0.wireOp",EDGE,"E4.filletArc")])],"isStart":true});
            var sketch = newSketch(context, id + "F18", { "sketchPlane" : qUnion([Q0])});
            skLineSegment(sketch, "E100.bottom", {"start": v(-23.7, -72) * mm, "end": v(115.3, -72) * mm});
            skLineSegment(sketch, "E100.top", {"start": v(-23.7, 1) * mm, "end": v(97.3, 1) * mm});
            skLineSegment(sketch, "E100.left", {"start": v(-28.7, -67) * mm, "end": v(-28.7, -4) * mm});
            skLineSegment(sketch, "E100.right", {"start": v(120.3, -67) * mm, "end": v(120.3, -14.51) * mm});
            skArc(sketch, "E101", {"start": v(132.17, 10.9) * mm, "mid": v(128.75, 22.22) * mm, "end": v(117.8, 17.77) * mm});
            skLineSegment(sketch, "E102", {"start": v(99.3, 3) * mm, "end": v(99.3, 9) * mm});
            skLineSegment(sketch, "E103", {"start": v(101.3, 11) * mm, "end": v(113.9, 11) * mm});
            skLineSegment(sketch, "E104", {"start": v(115.78, 12.3) * mm, "end": v(117.8, 17.77) * mm});
            skLineSegment(sketch, "E105", {"start": v(132.17, 10.9) * mm, "end": v(123.12, -4.27) * mm});
            skPoint(sketch, "E106.visualSharp", {"position": v(-28.7, 1) * mm});
            skArc(sketch, "E106.filletArc", {"start": v(-23.7, 1) * mm, "mid": v(-27.24, -0.46) * mm, "end": v(-28.7, -4) * mm});
            skPoint(sketch, "E107.visualSharp", {"position": v(-28.7, -72) * mm});
            skArc(sketch, "E107.filletArc", {"start": v(-28.7, -67) * mm, "mid": v(-27.24, -70.54) * mm, "end": v(-23.7, -72) * mm});
            skPoint(sketch, "E108.visualSharp", {"position": v(120.3, -72) * mm});
            skArc(sketch, "E108.filletArc", {"start": v(115.3, -72) * mm, "mid": v(118.84, -70.54) * mm, "end": v(120.3, -67) * mm});
            skPoint(sketch, "E109.visualSharp", {"position": v(99.3, 11) * mm});
            skArc(sketch, "E109.filletArc", {"start": v(101.3, 11) * mm, "mid": v(99.89, 10.41) * mm, "end": v(99.3, 9) * mm});
            skPoint(sketch, "E110.orphan", {"position": v(120.3, 1) * mm});
            skPoint(sketch, "E111.visualSharp", {"position": v(99.3, 1) * mm});
            skArc(sketch, "E111.filletArc", {"start": v(97.3, 1) * mm, "mid": v(98.71, 1.59) * mm, "end": v(99.3, 3) * mm});
            skPoint(sketch, "E112.visualSharp", {"position": v(120.3, -9) * mm});
            skArc(sketch, "E112.filletArc", {"start": v(123.12, -4.27) * mm, "mid": v(121.02, -9.2) * mm, "end": v(120.3, -14.51) * mm});
            skPoint(sketch, "E113.visualSharp", {"position": v(115.3, 11) * mm});
            skArc(sketch, "E113.filletArc", {"start": v(113.9, 11) * mm, "mid": v(115.05, 11.36) * mm, "end": v(115.78, 12.3) * mm});
            skLineSegment(sketch, "E114.0", {"start": v(132, 11) * mm, "end": v(122.95, -4.16) * mm});
            skArc(sketch, "E114.1", {"start": v(122.95, -4.16) * mm, "mid": v(120.83, -9.14) * mm, "end": v(120.1, -14.51) * mm});
            skLineSegment(sketch, "E114.2", {"start": v(120.1, -67) * mm, "end": v(120.1, -14.51) * mm});
            skArc(sketch, "E114.3", {"start": v(115.3, -71.8) * mm, "mid": v(118.7, -70.4) * mm, "end": v(120.1, -67) * mm});
            skLineSegment(sketch, "E114.4", {"start": v(-23.7, -71.8) * mm, "end": v(115.3, -71.8) * mm});
            skArc(sketch, "E114.5", {"start": v(101.3, 10.8) * mm, "mid": v(100.03, 10.27) * mm, "end": v(99.5, 9) * mm});
            skLineSegment(sketch, "E114.6", {"start": v(101.3, 10.8) * mm, "end": v(113.9, 10.8) * mm});
            skArc(sketch, "E114.7", {"start": v(113.9, 10.8) * mm, "mid": v(115.16, 11.2) * mm, "end": v(115.97, 12.24) * mm});
            skLineSegment(sketch, "E114.8", {"start": v(115.97, 12.24) * mm, "end": v(117.98, 17.7) * mm});
            skLineSegment(sketch, "E114.9", {"start": v(99.5, 3) * mm, "end": v(99.5, 9) * mm});
            skArc(sketch, "E114.10", {"start": v(97.3, 0.8) * mm, "mid": v(98.86, 1.44) * mm, "end": v(99.5, 3) * mm});
            skLineSegment(sketch, "E114.11", {"start": v(-23.7, 0.8) * mm, "end": v(97.3, 0.8) * mm});
            skArc(sketch, "E114.12", {"start": v(-23.7, 0.8) * mm, "mid": v(-27.1, -0.6) * mm, "end": v(-28.5, -4) * mm});
            skLineSegment(sketch, "E114.13", {"start": v(-28.5, -67) * mm, "end": v(-28.5, -4) * mm});
            skArc(sketch, "E114.14", {"start": v(132, 11) * mm, "mid": v(128.66, 22.04) * mm, "end": v(117.98, 17.7) * mm});
            skArc(sketch, "E114.15", {"start": v(-28.5, -67) * mm, "mid": v(-27.1, -70.4) * mm, "end": v(-23.7, -71.8) * mm});
            skSolve(sketch);
        }
        {
            var Q0;
            Q0=makeQuery(id+"F18.imprint","IMPRINT",FACE,{"disambiguationData":[TD([[makeQuery(id+"F18.imprint","IMPRINT",EDGE,{"derivedFrom":sQuery(id+"F18.wireOp",EDGE,"E114.0")}),-1.0]])]});
            extrude(context, id + "F19", {"entities" : qUnion([Q0]), "operationType" : NewBodyOperationType.REMOVE, "oppositeDirection" : true, "depth" : 38 * mm});
        }
        {
            var Q0;
            Q0=makeQuery(id+"F1.opExtrude","CAP_FACE",FACE,{"disambiguationData":[OSD([sQuery(id+"F0.wireOp",EDGE,"E0.bottom"),sQuery(id+"F0.wireOp",EDGE,"E0.top"),sQuery(id+"F0.wireOp",EDGE,"E0.left"),sQuery(id+"F0.wireOp",EDGE,"E0.right"),sQuery(id+"F0.wireOp",EDGE,"E1.filletArc"),sQuery(id+"F0.wireOp",EDGE,"E2.filletArc"),sQuery(id+"F0.wireOp",EDGE,"E3.filletArc"),sQuery(id+"F0.wireOp",EDGE,"E4.filletArc")])],"isStart":true});
            var sketch = newSketch(context, id + "F20", { "sketchPlane" : qUnion([Q0])});
            skLineSegment(sketch, "E115.bottom", {"start": v(-97, -63) * mm, "end": v(-84, -63) * mm});
            skLineSegment(sketch, "E115.top", {"start": v(-97, -16) * mm, "end": v(-84, -16) * mm});
            skLineSegment(sketch, "E115.left", {"start": v(-97, -63) * mm, "end": v(-97, -16) * mm});
            skLineSegment(sketch, "E115.right", {"start": v(-53, -63) * mm, "end": v(-53, -16) * mm});
            skArc(sketch, "E116", {"start": v(-66, -16) * mm, "mid": v(-75, -7) * mm, "end": v(-84, -16) * mm});
            skArc(sketch, "E117", {"start": v(-84, -63) * mm, "mid": v(-75, -72) * mm, "end": v(-66, -63) * mm});
            skLineSegment(sketch, "E118.trimOffspring", {"start": v(-66, -16) * mm, "end": v(-53, -16) * mm});
            skLineSegment(sketch, "E119.trimOffspring", {"start": v(-66, -63) * mm, "end": v(-53, -63) * mm});
            skLineSegment(sketch, "E120.0", {"start": v(-66.2, -16.2) * mm, "end": v(-53.2, -16.2) * mm});
            skLineSegment(sketch, "E120.1", {"start": v(-53.2, -62.8) * mm, "end": v(-53.2, -16.2) * mm});
            skArc(sketch, "E120.2", {"start": v(-66.2, -16.2) * mm, "mid": v(-75, -7.2) * mm, "end": v(-83.8, -16.2) * mm});
            skLineSegment(sketch, "E120.3", {"start": v(-66.2, -62.8) * mm, "end": v(-53.2, -62.8) * mm});
            skLineSegment(sketch, "E120.4", {"start": v(-96.8, -16.2) * mm, "end": v(-83.8, -16.2) * mm});
            skLineSegment(sketch, "E120.5", {"start": v(-96.8, -62.8) * mm, "end": v(-96.8, -16.2) * mm});
            skLineSegment(sketch, "E120.6", {"start": v(-96.8, -62.8) * mm, "end": v(-83.8, -62.8) * mm});
            skArc(sketch, "E120.7", {"start": v(-83.8, -62.8) * mm, "mid": v(-75, -71.8) * mm, "end": v(-66.2, -62.8) * mm});
            skSolve(sketch);
        }
        {
            var Q0;
            Q0=makeQuery(id+"F20.imprint","IMPRINT",FACE,{"disambiguationData":[TD([[makeQuery(id+"F20.imprint","IMPRINT",EDGE,{"derivedFrom":sQuery(id+"F20.wireOp",EDGE,"E120.0")}),-1.0]])]});
            extrude(context, id + "F21", {"entities" : qUnion([Q0]), "operationType" : NewBodyOperationType.REMOVE, "oppositeDirection" : true, "depth" : 38 * mm});
        }
    });
